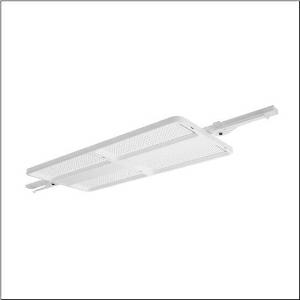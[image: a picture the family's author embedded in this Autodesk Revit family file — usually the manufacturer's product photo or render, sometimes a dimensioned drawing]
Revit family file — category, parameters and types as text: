
# Revit family: highbay_21_fur_modario_r__tragschiene_maxi_52hn12db4qma_08ca
name_source: partatom
category: Lighting Fixtures
units: mm (PartAtom-declared; Revit-internal decimal feet)

## family parameters
Cut with Voids When Loaded = No
Host = Face
Light Source = No
Part Type = Normal
Room Calculation Point = No
Round Connector Dimension = Use Diameter
Shared = No

## types (1)
- --- (1 x LED, 38000 lm, 197.7 W, 4000K)
    Apparent Load = 198 VA
    CIE Flux Codes = 90 98 100 100 100
    Color Rendering = 80
    Color Temperature = 4000K
    Default Elevation = 1800 mm
    Description = high bay luminaire Highbay 21 for Modario® trunking rail maxi; direct symmetric wide distribution, light control with lens of PMMA; UGR ≤ 22 (X = 4H | Y = 8H | S = 0.25H | reflection values 70/50/20); luminous flux: 38.000lm; light colour: 840, colour temperature: 4000K, MacAdam ≤ 3 SDCM (initial), colour rendering: CRI > 80; luminous efficacy: 192,2lm/W; rated service life: 75.000h (L80/B50) at AT= ta max; control: DALI 2; luminaire connection: plug, 5-pole, with phase selectionmains connection: 230..240V, AC 50/60Hz; connected load: 197,7W; protection rating (complete): IP64; insulation class (complete): insulation class I (protective earthing); protection symbol: D; impact resistance: IK07; certification: CE, ENEC, VDE, UKCA; internal wiring halogen-free; luminaire LABS conformity tested according to VDMA 24364:2018-05; corresponds to IFS (International Featured Standards) requirements for safety and quality in the food industry; housing frame of high-performance plastic PA6, matt traffic white (RAL 9016); cover of PMMA; fixing on rail side of steel, galvanised, white; blank cover of PC, traffic white (RAL 9016); dimension (LxWxH): 1.496 x 442 x 72mm; permissible operating ambient temperature: -35..+50°C (reducing of maximum allowable ambient temperature of 5°C with ceiling mounting); packaging unit: 1 piece
    Height = 72 mm  [stored 0.23622 ft]
    Lamp = 1 x LED
    Lamp Light Flux = 38000 lm
    Lamp Power = 197.7 W
    Lamp count = 1
    Length = 946 mm
    Luminous efficacy = 192 lm/W
    Manufacturer = Siteco
    ModVariant = No
    Model = 52HN12DB4QMA
    Mounting Place = Ceiling
    Mounting Type = Pendant
    Number of Poles = 1
    OnlyDefault = Yes
    Power Factor = 1
    Product Name = Highbay 21 für Modario® Tragschiene maxi
    Product group = high bay luminaire
    ProductGroupID = 901
    Protection Class = Protection class I
    Protection Degree = IP 64
    RLX_Detail_Level = 1
    RLX_Emergency_Light_Flux = 0 lm
    RLX_Emergency_Type = 0
    RLX_Emergency_Type_DB = No
    RlxData = <blob elided: 127309 chars, md5=0fba0ecc>
    Socket = socket
    Standby Power = 0 W
    System Light Flux = 38000 lm
    System Power = 198 W
    Type Comments = factory setting: luminous flux: 100 % | dim-lin: 254 | 918 mA
    Type Image = l_1363248.jpg
    URL = http://relux.com
    VarID = @adj_016241
    Voltage = 0 V
    Weight = 0.00 kg
    Width = 442 mm

note: [stored X ft] marks values corroborated as IEEE doubles in the binary element streams (Revit-internal decimal feet)

## geometry (parser evidence)
native form markers: Blend x4, Sweep x11
no freeform markers — native parametric forms only
